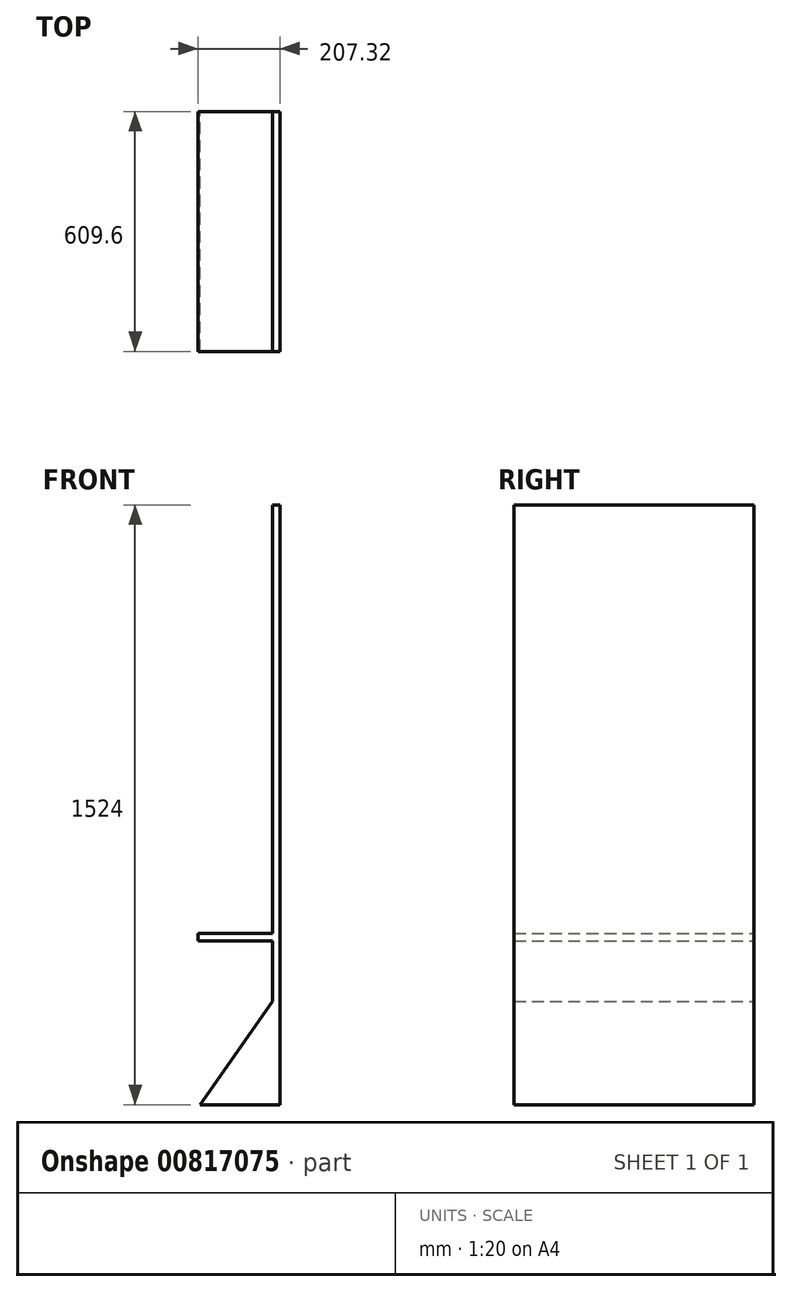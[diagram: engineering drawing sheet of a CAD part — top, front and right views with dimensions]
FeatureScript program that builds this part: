
annotation { "Feature Type Name" : "Feature", "Feature Type Description" : "" }
export const myFeature = defineFeature(function(context is Context, id is Id, definition is map)
    precondition{}
    {
        {
            var Q0;
            Q0=qCreatedBy(makeId("Front.planeOp"),FACE);
            var sketch = newSketch(context, id + "F0", { "sketchPlane" : qUnion([Q0])});
            skLineSegment(sketch, "E0", {"start": v(-24.72, 760.13) * mm, "end": v(-24.72, -763.87) * mm});
            skLineSegment(sketch, "E1", {"start": v(-24.72, -763.87) * mm, "end": v(-227.92, -763.87) * mm});
            skLineSegment(sketch, "E2", {"start": v(-227.92, -763.87) * mm, "end": v(-227.92, -763.87) * mm});
            skLineSegment(sketch, "E3", {"start": v(-24.72, -474.93) * mm, "end": v(-227.92, -763.87) * mm});
            skLineSegment(sketch, "E4", {"start": v(-24.72, -348.3) * mm, "end": v(-232.04, -348.3) * mm});
            skSolve(sketch);
        }
        {
            var Q0;
            {var subQ0=sQuery(id+"F0.wireOp",EDGE,"E1");Q0=makeQuery(id+"F0.imprint","IMPRINT",FACE,{"disambiguationData":[TD([[makeQuery(id+"F0.imprint","IMPRINT",EDGE,{"derivedFrom":subQ0}),-1.0]])]});}
            extrude(context, id + "F1", {"entities" : qUnion([Q0]), "depth" : 19.05 * mm, "offsetDistance" : 25.4 * mm});
        }
        {
            var Q0;
            Q0 = qSketchRegion(id + "F0", true);
            extrude(context, id + "F2", {"entities" : qUnion([Q0]), "operationType" : NewBodyOperationType.ADD, "depth" : 609.6 * mm, "offsetDistance" : 25.4 * mm});
        }
        {
            var Q0;
            Q0=sQuery(id+"F0.wireOp",EDGE,"E0");
            extrude(context, id + "F3", {"bodyType" : ToolBodyType.SURFACE, "surfaceEntities" : qUnion([Q0]), "depth" : 609.6 * mm, "offsetDistance" : 25.4 * mm});
        }
        {
            var Q0;
            Q0=makeQuery(id+"F3.opExtrude","SWEPT_FACE",FACE,{"disambiguationData":[OSD([sQuery(id+"F0.wireOp",EDGE,"E0")])]});
            extrude(context, id + "F4", {"entities" : qUnion([Q0]), "operationType" : NewBodyOperationType.ADD, "depth" : 19.05 * mm, "offsetDistance" : 25.4 * mm});
        }
        {
            var Q0;
            Q0 = qSketchRegion(id + "F0", true);
            extrude(context, id + "F5", {"entities" : qUnion([Q0]), "operationType" : NewBodyOperationType.ADD, "depth" : 25.4 * mm, "offsetDistance" : 25.4 * mm});
        }
        {
            var Q0;
            Q0=sQuery(id+"F0.wireOp",EDGE,"E4");
            extrude(context, id + "F6", {"bodyType" : ToolBodyType.SURFACE, "surfaceEntities" : qUnion([Q0]), "depth" : 609.6 * mm, "offsetDistance" : 25.4 * mm});
        }
        {
            var Q0;
            Q0=makeQuery(id+"F6.opExtrude","SWEPT_FACE",FACE,{"disambiguationData":[OSD([sQuery(id+"F0.wireOp",EDGE,"E4")])]});
            extrude(context, id + "F7", {"entities" : qUnion([Q0]), "operationType" : NewBodyOperationType.ADD, "depth" : 19.05 * mm, "offsetDistance" : 25.4 * mm});
        }
    });
